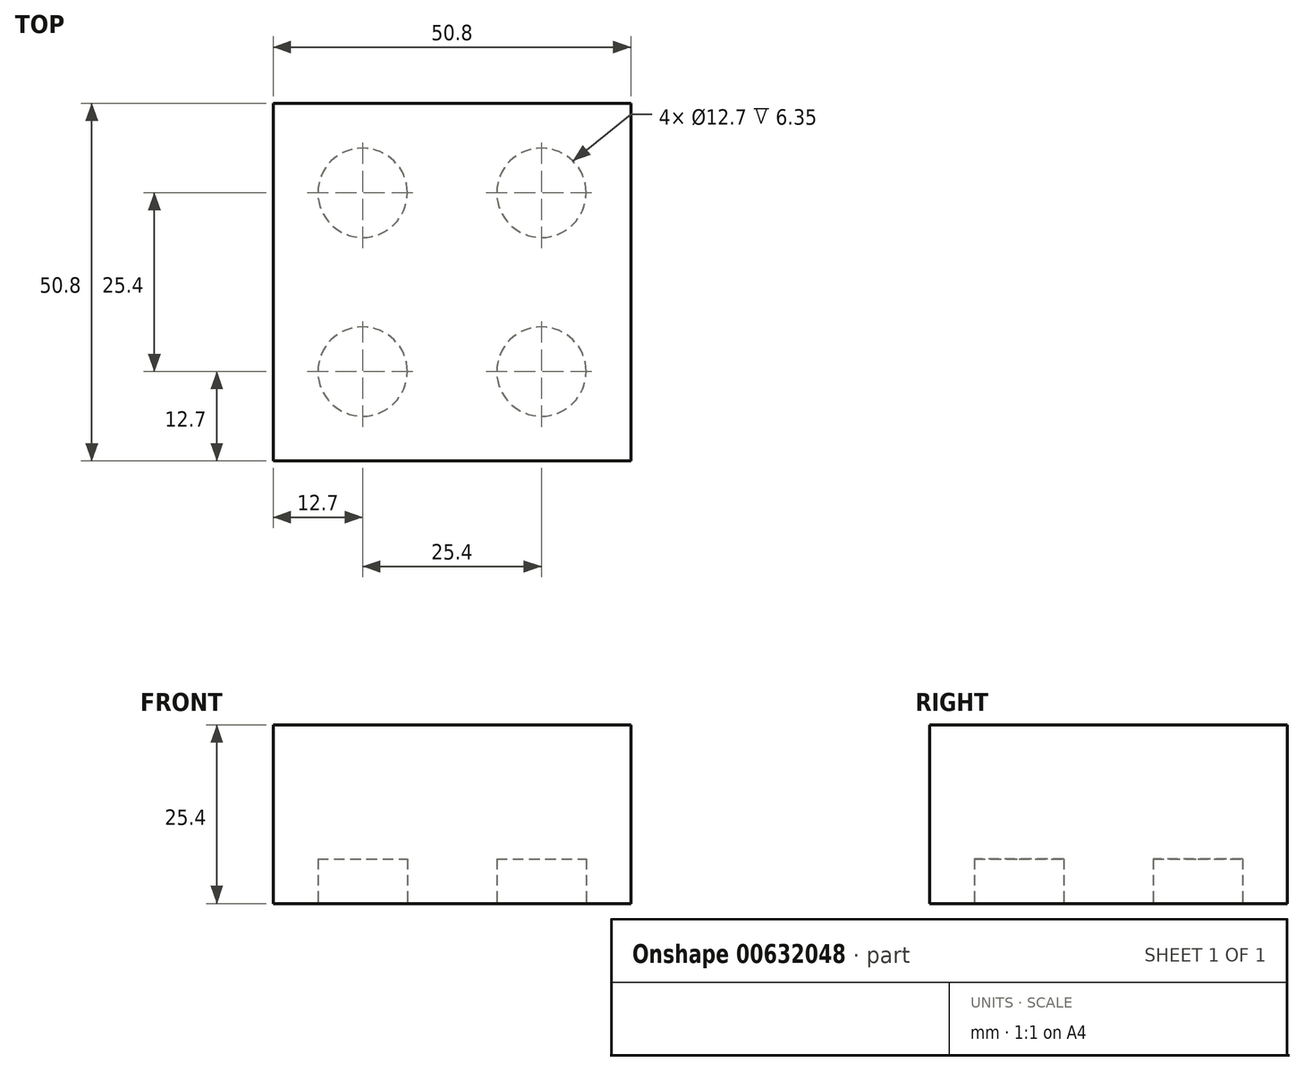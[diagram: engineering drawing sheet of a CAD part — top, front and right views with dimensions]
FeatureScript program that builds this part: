
annotation { "Feature Type Name" : "Feature", "Feature Type Description" : "" }
export const myFeature = defineFeature(function(context is Context, id is Id, definition is map)
    precondition{}
    {
        {
            var Q0;
            Q0=qCreatedBy(makeId("Front.planeOp"),FACE);
            var sketch = newSketch(context, id + "F0", { "sketchPlane" : qUnion([Q0])});
            skLineSegment(sketch, "E0.bottom", {"start": v(0, 0) * mm, "end": v(50.8, 0) * mm});
            skLineSegment(sketch, "E0.top", {"start": v(0, 25.4) * mm, "end": v(50.8, 25.4) * mm});
            skLineSegment(sketch, "E0.left", {"start": v(0, 0) * mm, "end": v(0, 25.4) * mm});
            skLineSegment(sketch, "E0.right", {"start": v(50.8, 0) * mm, "end": v(50.8, 25.4) * mm});
            skSolve(sketch);
        }
        {
            var Q0;
            Q0 = qSketchRegion(id + "F0", true);
            extrude(context, id + "F1", {"entities" : qUnion([Q0]), "depth" : 50.8 * mm, "offsetDistance" : 25.4 * mm});
        }
        {
            var Q0;
            Q0=makeQuery(id+"F1.opExtrude","SWEPT_FACE",FACE,{"disambiguationData":[OSD([sQuery(id+"F0.wireOp",EDGE,"E0.bottom")])]});
            var sketch = newSketch(context, id + "F2", { "sketchPlane" : qUnion([Q0])});
            skCircle(sketch, "E1", {"center": v(12.7, 38.1) * mm, "radius": 6.35 * mm});
            skCircle(sketch, "E2", {"center": v(12.7, 12.7) * mm, "radius": 6.35 * mm});
            skCircle(sketch, "E3", {"center": v(38.1, 12.7) * mm, "radius": 6.35 * mm});
            skCircle(sketch, "E4", {"center": v(38.1, 38.1) * mm, "radius": 6.35 * mm});
            skSolve(sketch);
        }
        {
            var Q0;
            Q0 = qSketchRegion(id + "F2", true);
            extrude(context, id + "F3", {"entities" : qUnion([Q0]), "operationType" : NewBodyOperationType.REMOVE, "oppositeDirection" : true, "depth" : 6.35 * mm, "offsetDistance" : 25.4 * mm});
        }
    });
